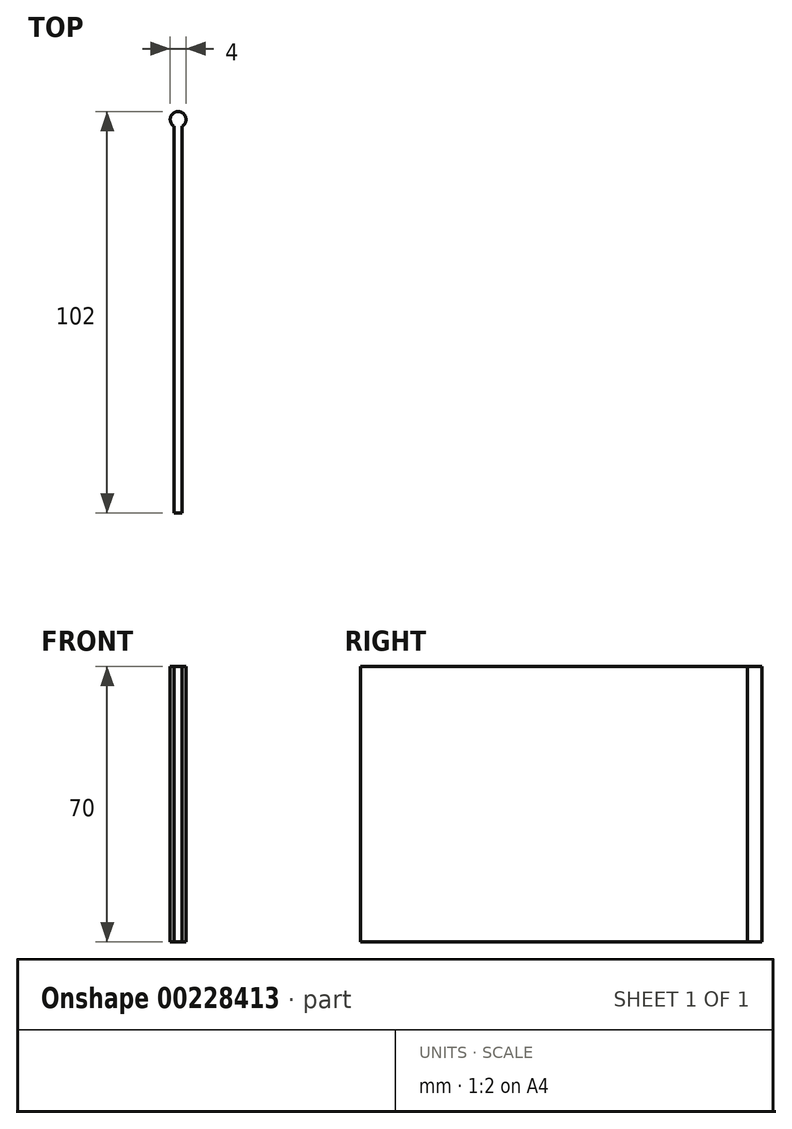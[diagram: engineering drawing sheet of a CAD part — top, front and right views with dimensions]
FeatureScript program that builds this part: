
annotation { "Feature Type Name" : "Feature", "Feature Type Description" : "" }
export const myFeature = defineFeature(function(context is Context, id is Id, definition is map)
    precondition{}
    {
        {
            var Q0;
            Q0=qCreatedBy(makeId("Front.planeOp"),FACE);
            var sketch = newSketch(context, id + "F0", { "sketchPlane" : qUnion([Q0])});
            skLineSegment(sketch, "E0.bottom", {"start": v(1, 0) * mm, "end": v(-1, 0) * mm});
            skLineSegment(sketch, "E0.top", {"start": v(1, 70) * mm, "end": v(-1, 70) * mm});
            skLineSegment(sketch, "E0.left", {"start": v(1, 0) * mm, "end": v(1, 70) * mm});
            skLineSegment(sketch, "E0.right", {"start": v(-1, 0) * mm, "end": v(-1, 70) * mm});
            skSolve(sketch);
        }
        {
            var Q0;
            Q0 = qSketchRegion(id + "F0", true);
            extrude(context, id + "F1", {"entities" : qUnion([Q0]), "depth" : 100 * mm});
        }
        {
            var Q0;
            Q0=makeQuery(id+"F1.opExtrude","SWEPT_FACE",FACE,{"disambiguationData":[OSD([sQuery(id+"F0.wireOp",EDGE,"E0.top")])]});
            var sketch = newSketch(context, id + "F2", { "sketchPlane" : qUnion([Q0])});
            skCircle(sketch, "E1", {"center": v(0, 0) * mm, "radius": 2 * mm});
            skSolve(sketch);
        }
        {
            var Q0;
            {var subQ1=sQuery(id+"F0.wireOp",EDGE,"E0.top");var subQ6=makeQuery(id+"F1.opExtrude","CAP_EDGE",EDGE,{"disambiguationData":[OSD([subQ1])],"isStart":true});Q0=makeQuery(id+"F2.imprint","IMPRINT",FACE,{"disambiguationData":[TD([[makeQuery(id+"F2.imprint","IMPRINT",EDGE,{"derivedFrom":subQ6}),-1.0]])]});}
            var Q1;
            Q1=makeQuery(id+"F1.opExtrude","SWEPT_FACE",FACE,{"disambiguationData":[OSD([sQuery(id+"F0.wireOp",EDGE,"E0.bottom")])]});
            extrude(context, id + "F3", {"entities" : qUnion([Q0]), "operationType" : NewBodyOperationType.ADD, "endBound" : BoundingType.UP_TO_SURFACE, "oppositeDirection" : true, "endBoundEntityFace" : qUnion([Q1]), "depth" : 25 * mm});
        }
    });
